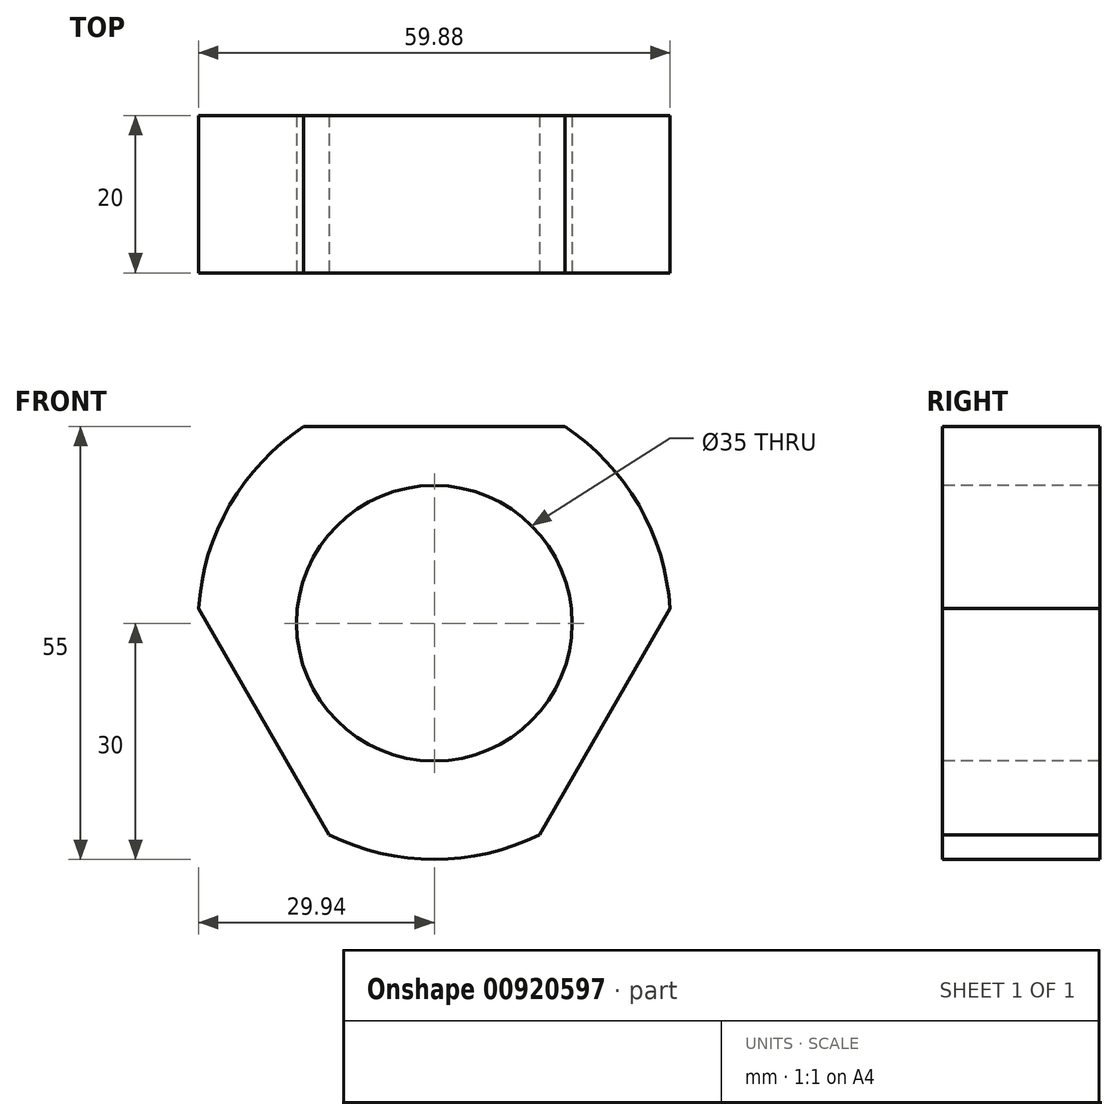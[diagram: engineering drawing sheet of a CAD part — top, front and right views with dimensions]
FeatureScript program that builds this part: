
annotation { "Feature Type Name" : "Feature", "Feature Type Description" : "" }
export const myFeature = defineFeature(function(context is Context, id is Id, definition is map)
    precondition{}
    {
        {
            var Q0;
            Q0=qCreatedBy(makeId("Front.planeOp"),FACE);
            var sketch = newSketch(context, id + "F0", { "sketchPlane" : qUnion([Q0])});
            skCircle(sketch, "E0", {"center": v(0, 0) * mm, "radius": 30 * mm});
            skCircle(sketch, "E1", {"center": v(0, 0) * mm, "radius": 17.5 * mm});
            skSolve(sketch);
        }
        {
            var Q0;
            Q0 = qSketchRegion(id + "F0", true);
            extrude(context, id + "F1", {"entities" : qUnion([Q0]), "oppositeDirection" : true, "depth" : 20 * mm, "offsetDistance" : 25 * mm});
        }
        {
            var Q0;
            Q0=makeQuery(id+"F1.opExtrude","CAP_FACE",FACE,{"disambiguationData":[OSD([sQuery(id+"F0.wireOp",EDGE,"E0"),sQuery(id+"F0.wireOp",EDGE,"E1")])],"isStart":true});
            var sketch = newSketch(context, id + "F2", { "sketchPlane" : qUnion([Q0])});
            skCircle(sketch, "E2.0", {"center": v(0, 0) * mm, "radius": 17.5 * mm});
            skCircle(sketch, "E3.0", {"center": v(0, 0) * mm, "radius": 30 * mm});
            skCircle(sketch, "E4.cCircle", {"center": v(0, 0) * mm, "radius": 25 * mm, "construction": true});
            skLineSegment(sketch, "E4.0", {"start": v(-43.3, 25) * mm, "end": v(43.3, 25) * mm});
            skLineSegment(sketch, "E4.1", {"start": v(43.3, 25) * mm, "end": v(0, -50) * mm});
            skLineSegment(sketch, "E4.2", {"start": v(0, -50) * mm, "end": v(-43.3, 25) * mm});
            skPoint(sketch, "E4.0.midPoint", {"position": v(0, 25) * mm});
            skCircle(sketch, "E5", {"center": v(0, 0) * mm, "radius": 100 * mm});
            skSolve(sketch);
        }
        {
            var Q0;
            Q0=makeQuery(id+"F2.imprint","IMPRINT",FACE,{"disambiguationData":[TD([[makeQuery(id+"F2.imprint","IMPRINT",EDGE,{"derivedFrom":sQuery(id+"F2.wireOp",EDGE,"E5")}),1.0]])]});
            var Q1;
            {var subQ0=sQuery(id+"F2.wireOp",EDGE,"E4.0");var subQ1=sQuery(id+"F2.wireOp",EDGE,"E3.0");var subQ2=makeQuery(id+"F2.imprint","INTERSECT",VERTEX,{"disambiguationData":[OD(0.0)],"derivedFrom":[subQ1,subQ0]});Q1=makeQuery(id+"F2.imprint","IMPRINT",FACE,{"disambiguationData":[TD([[makeQuery(id+"F2.imprint","IMPRINT",EDGE,{"disambiguationData":[TD([[subQ2,-1.0]])],"derivedFrom":subQ1}),1.0]])]});}
            var Q2;
            {var subQ0=sQuery(id+"F2.wireOp",EDGE,"E4.2");var subQ1=sQuery(id+"F2.wireOp",EDGE,"E3.0");var subQ2=makeQuery(id+"F2.imprint","INTERSECT",VERTEX,{"disambiguationData":[OD(0.0)],"derivedFrom":[subQ1,subQ0]});Q2=makeQuery(id+"F2.imprint","IMPRINT",FACE,{"disambiguationData":[TD([[makeQuery(id+"F2.imprint","IMPRINT",EDGE,{"disambiguationData":[TD([[subQ2,-1.0]])],"derivedFrom":subQ1}),1.0]])]});}
            var Q3;
            {var subQ0=sQuery(id+"F2.wireOp",EDGE,"E4.1");var subQ1=sQuery(id+"F2.wireOp",EDGE,"E3.0");var subQ2=makeQuery(id+"F2.imprint","INTERSECT",VERTEX,{"disambiguationData":[OD(0.0)],"derivedFrom":[subQ1,subQ0]});Q3=makeQuery(id+"F2.imprint","IMPRINT",FACE,{"disambiguationData":[TD([[makeQuery(id+"F2.imprint","IMPRINT",EDGE,{"disambiguationData":[TD([[subQ2,1.0]])],"derivedFrom":subQ1}),1.0]])]});}
            extrude(context, id + "F3", {"entities" : qUnion([Q0, Q1, Q2, Q3]), "operationType" : NewBodyOperationType.REMOVE, "endBound" : BoundingType.THROUGH_ALL, "oppositeDirection" : true, "depth" : 25 * mm, "offsetDistance" : 25 * mm});
        }
    });
